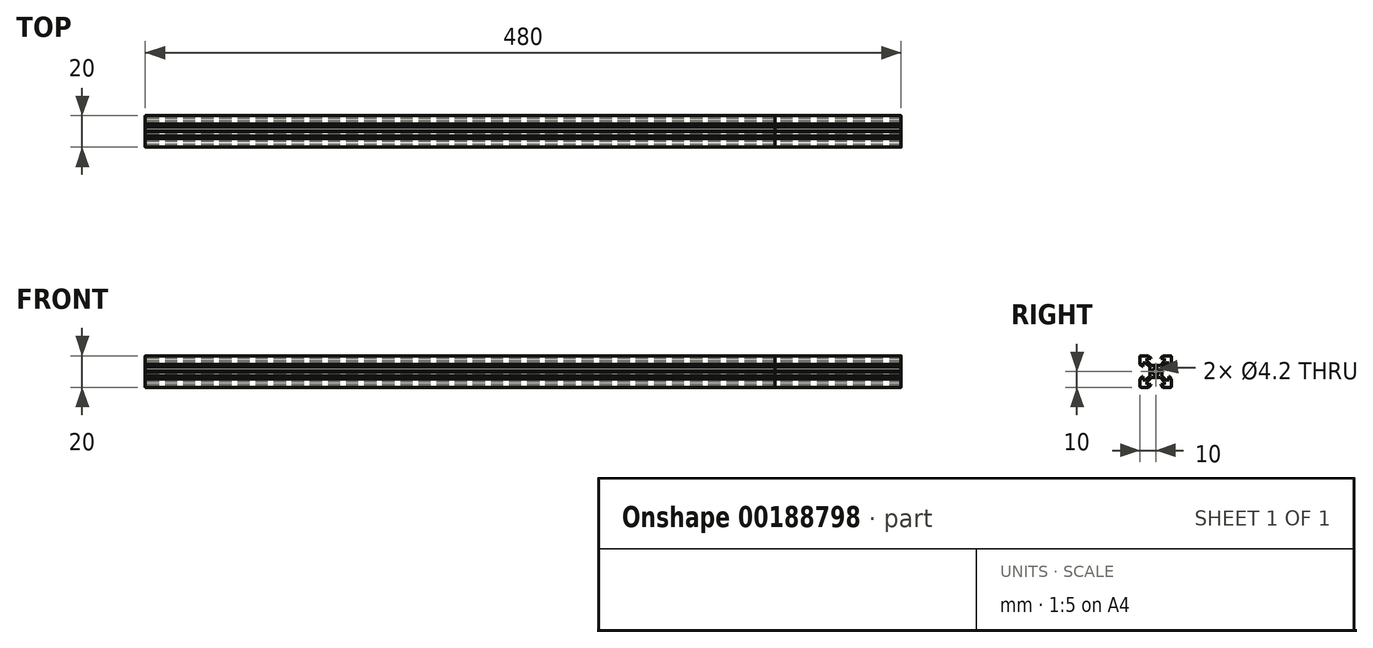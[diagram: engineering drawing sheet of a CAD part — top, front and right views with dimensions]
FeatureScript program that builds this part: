
annotation { "Feature Type Name" : "Feature", "Feature Type Description" : "" }
export const myFeature = defineFeature(function(context is Context, id is Id, definition is map)
    precondition{}
    {
        {
            var Q0;
            Q0=qCreatedBy(makeId("Right.planeOp"),FACE);
            var sketch = newSketch(context, id + "F0", { "sketchPlane" : qUnion([Q0])});
            skArc(sketch, "E0", {"start": v(-10, -9.5) * mm, "mid": v(-9.85, -9.85) * mm, "end": v(-9.5, -10) * mm});
            skCircle(sketch, "E1", {"center": v(0, 0) * mm, "radius": 2.1 * mm});
            skArc(sketch, "E2", {"start": v(-9.5, 10) * mm, "mid": v(-9.85, 9.85) * mm, "end": v(-10, 9.5) * mm});
            skLineSegment(sketch, "E3", {"start": v(-3.69, 0) * mm, "end": v(-3.9, -0.2) * mm});
            skLineSegment(sketch, "E4", {"start": v(-3.9, -0.21) * mm, "end": v(-3.9, -2.84) * mm});
            skLineSegment(sketch, "E5", {"start": v(-3.9, -2.84) * mm, "end": v(-6.56, -5.5) * mm});
            skLineSegment(sketch, "E6", {"start": v(-6.56, -5.5) * mm, "end": v(-8.2, -5.5) * mm});
            skLineSegment(sketch, "E7", {"start": v(-8.2, -5.5) * mm, "end": v(-8.2, -3.12) * mm});
            skLineSegment(sketch, "E8", {"start": v(-8.2, -3.12) * mm, "end": v(-8.54, -3.12) * mm});
            skLineSegment(sketch, "E9", {"start": v(-8.54, -3.12) * mm, "end": v(-10, -4.58) * mm});
            skLineSegment(sketch, "E10", {"start": v(-10, -9.5) * mm, "end": v(-10, -4.58) * mm});
            skLineSegment(sketch, "E11", {"start": v(-9.5, -10) * mm, "end": v(-4.58, -10) * mm});
            skLineSegment(sketch, "E12", {"start": v(-3.12, -8.54) * mm, "end": v(-4.58, -10) * mm});
            skLineSegment(sketch, "E13", {"start": v(-3.12, -8.2) * mm, "end": v(-3.12, -8.54) * mm});
            skLineSegment(sketch, "E14", {"start": v(-5.5, -8.2) * mm, "end": v(-3.12, -8.2) * mm});
            skLineSegment(sketch, "E15", {"start": v(-5.5, -6.56) * mm, "end": v(-5.5, -8.2) * mm});
            skLineSegment(sketch, "E16", {"start": v(-2.84, -3.9) * mm, "end": v(-5.5, -6.56) * mm});
            skLineSegment(sketch, "E17", {"start": v(-0.21, -3.9) * mm, "end": v(-2.84, -3.9) * mm});
            skLineSegment(sketch, "E18", {"start": v(0, -3.69) * mm, "end": v(-0.2, -3.9) * mm});
            skLineSegment(sketch, "E19", {"start": v(0, -3.69) * mm, "end": v(0.2, -3.9) * mm});
            skLineSegment(sketch, "E20", {"start": v(0.21, -3.9) * mm, "end": v(2.84, -3.9) * mm});
            skLineSegment(sketch, "E21", {"start": v(2.84, -3.9) * mm, "end": v(5.5, -6.56) * mm});
            skLineSegment(sketch, "E22", {"start": v(5.5, -6.56) * mm, "end": v(5.5, -8.2) * mm});
            skLineSegment(sketch, "E23", {"start": v(5.5, -8.2) * mm, "end": v(3.12, -8.2) * mm});
            skLineSegment(sketch, "E24", {"start": v(3.12, -8.2) * mm, "end": v(3.12, -8.54) * mm});
            skLineSegment(sketch, "E25", {"start": v(3.12, -8.54) * mm, "end": v(4.58, -10) * mm});
            skLineSegment(sketch, "E26", {"start": v(4.58, -10) * mm, "end": v(9.5, -10) * mm});
            skArc(sketch, "E27", {"start": v(9.5, -10) * mm, "mid": v(9.85, -9.85) * mm, "end": v(10, -9.5) * mm});
            skLineSegment(sketch, "E28", {"start": v(10, -9.5) * mm, "end": v(10, -4.58) * mm});
            skLineSegment(sketch, "E29", {"start": v(8.54, -3.12) * mm, "end": v(10, -4.58) * mm});
            skLineSegment(sketch, "E30", {"start": v(8.2, -3.12) * mm, "end": v(8.54, -3.12) * mm});
            skLineSegment(sketch, "E31", {"start": v(8.2, -5.5) * mm, "end": v(8.2, -3.12) * mm});
            skLineSegment(sketch, "E32", {"start": v(6.56, -5.5) * mm, "end": v(8.2, -5.5) * mm});
            skLineSegment(sketch, "E33", {"start": v(3.9, -2.84) * mm, "end": v(6.56, -5.5) * mm});
            skLineSegment(sketch, "E34", {"start": v(3.9, -0.21) * mm, "end": v(3.9, -2.84) * mm});
            skLineSegment(sketch, "E35", {"start": v(3.69, 0) * mm, "end": v(3.9, -0.2) * mm});
            skLineSegment(sketch, "E36", {"start": v(3.69, 0) * mm, "end": v(3.9, 0.2) * mm});
            skLineSegment(sketch, "E37", {"start": v(3.9, 0.21) * mm, "end": v(3.9, 2.84) * mm});
            skLineSegment(sketch, "E38", {"start": v(3.9, 2.84) * mm, "end": v(6.56, 5.5) * mm});
            skLineSegment(sketch, "E39", {"start": v(6.56, 5.5) * mm, "end": v(8.2, 5.5) * mm});
            skLineSegment(sketch, "E40", {"start": v(8.2, 5.5) * mm, "end": v(8.2, 3.12) * mm});
            skLineSegment(sketch, "E41", {"start": v(8.2, 3.12) * mm, "end": v(8.54, 3.12) * mm});
            skLineSegment(sketch, "E42", {"start": v(8.54, 3.12) * mm, "end": v(10, 4.58) * mm});
            skLineSegment(sketch, "E43", {"start": v(10, 4.58) * mm, "end": v(10, 9.5) * mm});
            skArc(sketch, "E44", {"start": v(10, 9.5) * mm, "mid": v(9.85, 9.85) * mm, "end": v(9.5, 10) * mm});
            skLineSegment(sketch, "E45", {"start": v(4.58, 10) * mm, "end": v(9.5, 10) * mm});
            skLineSegment(sketch, "E46", {"start": v(3.12, 8.54) * mm, "end": v(4.58, 10) * mm});
            skLineSegment(sketch, "E47", {"start": v(3.12, 8.2) * mm, "end": v(3.12, 8.54) * mm});
            skLineSegment(sketch, "E48", {"start": v(5.5, 8.2) * mm, "end": v(3.12, 8.2) * mm});
            skLineSegment(sketch, "E49", {"start": v(5.5, 6.56) * mm, "end": v(5.5, 8.2) * mm});
            skLineSegment(sketch, "E50", {"start": v(2.84, 3.9) * mm, "end": v(5.5, 6.56) * mm});
            skLineSegment(sketch, "E51", {"start": v(0.21, 3.9) * mm, "end": v(2.84, 3.9) * mm});
            skLineSegment(sketch, "E52", {"start": v(0, 3.69) * mm, "end": v(0.2, 3.9) * mm});
            skLineSegment(sketch, "E53", {"start": v(0, 3.69) * mm, "end": v(-0.2, 3.9) * mm});
            skLineSegment(sketch, "E54", {"start": v(-0.21, 3.9) * mm, "end": v(-2.84, 3.9) * mm});
            skLineSegment(sketch, "E55", {"start": v(-2.84, 3.9) * mm, "end": v(-5.5, 6.56) * mm});
            skLineSegment(sketch, "E56", {"start": v(-5.5, 6.56) * mm, "end": v(-5.5, 8.2) * mm});
            skLineSegment(sketch, "E57", {"start": v(-5.5, 8.2) * mm, "end": v(-3.12, 8.2) * mm});
            skLineSegment(sketch, "E58", {"start": v(-3.12, 8.2) * mm, "end": v(-3.12, 8.54) * mm});
            skLineSegment(sketch, "E59", {"start": v(-3.12, 8.54) * mm, "end": v(-4.58, 10) * mm});
            skLineSegment(sketch, "E60", {"start": v(-9.5, 10) * mm, "end": v(-4.58, 10) * mm});
            skLineSegment(sketch, "E61", {"start": v(-10, 4.58) * mm, "end": v(-10, 9.5) * mm});
            skLineSegment(sketch, "E62", {"start": v(-8.54, 3.12) * mm, "end": v(-10, 4.58) * mm});
            skLineSegment(sketch, "E63", {"start": v(-8.2, 3.12) * mm, "end": v(-8.54, 3.12) * mm});
            skLineSegment(sketch, "E64", {"start": v(-8.2, 5.5) * mm, "end": v(-8.2, 3.12) * mm});
            skLineSegment(sketch, "E65", {"start": v(-6.56, 5.5) * mm, "end": v(-8.2, 5.5) * mm});
            skLineSegment(sketch, "E66", {"start": v(-3.9, 2.84) * mm, "end": v(-6.56, 5.5) * mm});
            skLineSegment(sketch, "E67", {"start": v(-3.9, 0.21) * mm, "end": v(-3.9, 2.84) * mm});
            skLineSegment(sketch, "E68", {"start": v(-3.69, 0) * mm, "end": v(-3.9, 0.2) * mm});
            skSolve(sketch);
        }
        {
            var Q0;
            Q0=makeQuery(id+"F0.imprint","IMPRINT",FACE,{"disambiguationData":[TD([[makeQuery(id+"F0.imprint","IMPRINT",EDGE,{"derivedFrom":sQuery(id+"F0.wireOp",EDGE,"E0")}),1.0]])]});
            extrude(context, id + "F1", {"entities" : qUnion([Q0]), "depth" : (456 - 56.2) * mm});
        }
        {
            var Q0;
            Q0 = qSketchRegion(id + "F0", true);
            extrude(context, id + "F2", {"entities" : qUnion([Q0]), "depth" : 480 * mm, "offsetDistance" : 25 * mm});
        }
    });
